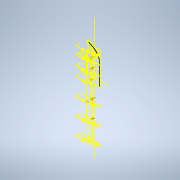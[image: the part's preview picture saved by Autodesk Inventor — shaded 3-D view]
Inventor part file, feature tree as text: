
AUTODESK INVENTOR PART (.ipt)
format: ipt  version: 2020.3 (Build 243373010, 373A)  size: 272,896 bytes
history: native  units: mm
features: other x49, sketch x10, surface_op x2
ambient origin geometry x8: Origin, YZ Plane, XZ Plane, XY Plane, X Axis, Y Axis, Z Axis, Center Point
bodies: Body1 (feature_tree), Body2 (feature_tree)
feature tree (61):
  other  "base_sketch.ipt"
  other  "side_liner_plane"
  other  "top_liner"
  other  "side_liner"
  other  "bottom_liner"
  other  "front_plane"
  other  "liner_side_bottom"
  other  "stringer"
  other  "stringer_inside"
  other  "bulkhead_main"
  other  "bulkhead_F1"
  other  "bulkhead_front"
  other  "bulkhead_F2"
  other  "bulkhead_B1"
  other  "bulkhead_B2"
  other  "transom"
  other  "bulkhead_main_plane"
  other  "bulkhead_front_plane"
  other  "bulkhead_F1_plane"
  other  "front_tip_plane"
  other  "bulkhead_F2_plane"
  other  "bulkhead_B1_plane"
  other  "bulkhead_B2_plane"
  other  "transom_plane"
  other  "bulkhead_front_tunnel_top"
  other  "bulkhead_front_tunnel_bottom"
  other  "bulkhead_main_top"
  other  "bulkhead_main_tunnel_bottom"
  other  "bulkhead_main_tunnel_standoff"
  other  "bulkhead_front_top"
  other  "bulkhead_front_bottom"
  other  "bulkhead_F1_tunnel_bottom"
  other  "bulkhead_F1_tunnel_top"
  other  "bulkhead_F1_top"
  other  "bulkhead_F1_tunnel_standoff"
  other  "bulkhead_F1_bottom"
  other  "bulkhead_F2_bottom"
  other  "bulkhead_F2_top"
  other  "bulkhead_B1_bottom"
  other  "bulkhead_B1_top"
  other  "bulkhead_B1_tunnel_standoff"
  other  "bulkhead_B1_tunnel_bottom"
  other  "bulkhead_B2_top"
  other  "bulkhead_B2_tunnel_bottom"
  other  "bulkhead_B2_bottom"
  sketch  "Sketch16"  dims[d0=10.0mm]
  sketch  "Sketch17"  dims[d30=306.0mm d49=45.9mm d55=57.528mm d64=19.176mm d65=18.36mm d96=34.468504mm d99=12.202833mm d107=12.202833mm d109=3.582087mm d120=21.382716mm d122=1.094773mm d125=3.585707mm d128=6.375647mm d130=57.528mm d136=2.48676mm]
  sketch  "Sketch18"  dims[d2=35.7mm d3=20.4mm d7=204.0mm d24=45.9mm d27=11.475mm d41=45.9mm d44=0.698132mm d45=122.4mm d48=27.54mm d50=49.7352mm d51=43.146mm d53=62.322mm d54=119.85mm d56=34.5168mm d57=11.5056mm d58=2.48676mm d61=33.558mm d63=0.918mm d66=62.322mm d67=19.176mm d68=19.176mm d70=9.18mm d71=15.0552mm d84=153.0mm d85=41.6925mm d86=102.0mm d87=42.84mm d90=40.8mm d91=24.48mm d95=10.2mm d97=10.340551mm d98=15.510827mm d100=8.541983mm d101=2.55mm d103=112.2mm d104=6.40305mm d105=6.885mm d106=17.2125mm d108=12.202833mm d110=3.582087mm d111=-102.0mm d112=-204.0mm d114=6.981317mm d115=6.981317mm d116=6.981317mm d119=11.760494mm d121=3.635062mm d123=0.729849mm d124=0.364924mm d126=2.390472mm d127=1.195236mm d131=48.8988mm d137=1.86507mm]
  sketch  "Sketch19"  dims[d35=21.346493mm]
  sketch  "Sketch21"  dims[d36=32.019739mm]
  other  "Srf2"
  sketch  "Sketch22"  dims[d59=0.0mm d60=90.0deg]
  sketch  "Sketch23"  dims[d62=0.0mm d69=90.0deg]
  sketch  "Sketch24"  dims[d72=0.0mm d73=90.0deg]
  sketch  "Sketch25"  dims[d74=0.0mm d75=90.0deg]
  sketch  "Sketch26"  dims[d76=0.0mm d77=90.0deg d78=0.0mm d79=90.0deg d80=0.0mm d81=90.0deg d82=0.0mm d83=90.0deg d88=0.0mm d89=90.0deg d92=0.0mm d93=90.0deg d113=0.0mm d117=90.0deg d118=0.0mm d129=90.0deg]
  other  "stinger_bottom_liner"
  other  "Srf3"
  surface_op  "surface_side"
  surface_op  "surface_bottom"
  other  "3D Intersection1"
